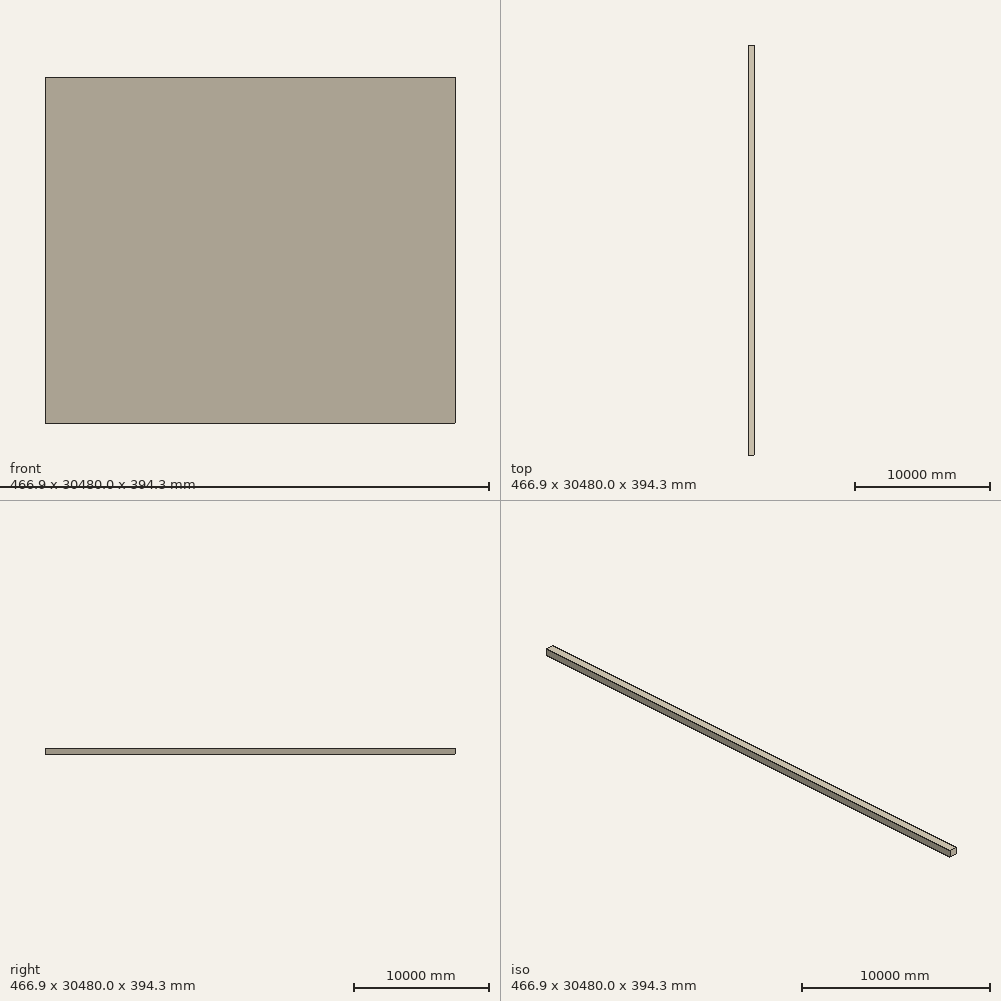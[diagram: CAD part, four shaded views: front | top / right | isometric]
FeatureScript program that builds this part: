
annotation { "Feature Type Name" : "Feature", "Feature Type Description" : "" }
export const myFeature = defineFeature(function(context is Context, id is Id, definition is map)
    precondition{}
    {
        {
            var Q0;
            Q0=qCreatedBy(makeId("Front.planeOp"),FACE);
            var sketch = newSketch(context, id + "F0", { "sketchPlane" : qUnion([Q0])});
            skLineSegment(sketch, "E0.bottom", {"start": v(233.45, 197.15) * mm, "end": v(-233.45, 197.15) * mm});
            skLineSegment(sketch, "E0.top", {"start": v(233.45, -197.15) * mm, "end": v(-233.45, -197.15) * mm});
            skLineSegment(sketch, "E0.left", {"start": v(233.45, 197.15) * mm, "end": v(233.45, -197.15) * mm});
            skLineSegment(sketch, "E0.right", {"start": v(-233.45, 197.15) * mm, "end": v(-233.45, -197.15) * mm});
            skPoint(sketch, "E0.middle", {"position": v(0, 0) * mm});
            skSolve(sketch);
        }
        {
            var Q0;
            Q0 = qSketchRegion(id + "F0", true);
            extrude(context, id + "F1", {"entities" : qUnion([Q0]), "endBound" : BoundingType.SYMMETRIC, "depth" : 30480 * mm, "offsetDistance" : 25.4 * mm});
        }
    });
